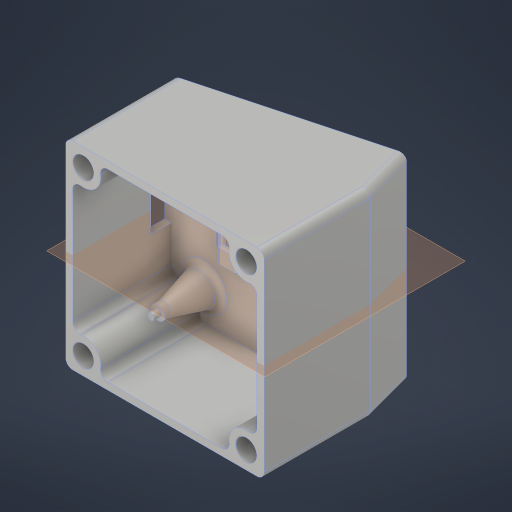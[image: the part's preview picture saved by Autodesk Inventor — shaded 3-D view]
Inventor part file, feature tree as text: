
AUTODESK INVENTOR PART (.ipt)
format: ipt  version: 2023 (Build 270158000, 158)  size: 456,192 bytes
history: native  units: in
note: dims shown in document units (in); Inventor stores cm internally (conversion verified against a paired STEP export)
features: sketch x8, extrude x8, projected_geometry x4, fillet x2, chamfer x2, hole x1, mirror x1, shell x1, plane x1
ambient origin geometry x8: Origin, YZ Plane, XZ Plane, XY Plane, X Axis, Y Axis, Z Axis, Center Point
bodies: Solid1 (feature_tree)
feature tree (28):
  sketch  "Sketch1"  dims[d0=1.4961in d1=1.4961in]
  extrude  "Extrusion1"  Depth=1.4961in
  hole  "Hole1"  [1 undecoded]
  extrude  "Extrusion6"  Depth=0.0787in
  mirror  "Mirror1"
  shell  "Shell1"  Thickness=0.3937in
  extrude  "Extrusion7"  Depth=0.0787in
  fillet  "Fillet1"  Radius=0.1575in
  extrude  "Extrusion2"  Depth=0.1575in
  chamfer  "Chamfer1"  Distance=0.5906in
  extrude  "Extrusion3"  Depth=0.315in
  sketch  "Sketch3"  dims[d5=1.1811in d6=0.0in d7=0.0787in d8=0.3937in]
  extrude  "Extrusion4"  Depth=0.315in
  plane  "Work Plane1"
  extrude  "Extrusion5"  Depth=0.315in
  chamfer  "Chamfer2"  Distance=0.0748in
  fillet  "Fillet3"  Radius=0.0787in
  extrude  "Extrusion8"  Depth=0.315in
  sketch  "Sketch2"  dims[d2=1.3386in d3=1.3386in]
  projected_geometry  "Projected Loop1"
  projected_geometry  "Projected Loop2"
  projected_geometry  "Projected Loop3"
  sketch  "Sketch4"  dims[d9=1.811in]
  sketch  "Sketch5"  dims[d10=0.2283in d11=0.2362in d12=0.385in d13=0.0787in d14=0.5635in d15=0.315in d16=0.8108in d17=0.0787in d18=0.1575in]
  sketch  "Sketch6"  dims[d19=0.1575in d20=0.1575in]
  sketch  "Sketch9"  dims[d21=0.1575in d22=0.5906in d23=0.0in]
  sketch  "Sketch10"  dims[d24=0.1181in d25=0.0787in d26=75.0deg d27=0.0748in d28=0.0748in d29=0.0748in d30=0.0748in d31=0.0787in d32=0.0in d33=0.4724in d34=0.2362in d35=0.0787in d36=1.1811in d37=0.0in d42=0.1969in d43=0.0in d44=0.0197in d45=0.0787in d46=0.481in d47=0.2283in d48=0.2283in d49=0.1969in d50=1.0in d51=0.2756in d52=0.0in d61=0.0787in d62=15.0deg d63=0.3937in d64=0.0in d65=0.0591in d66=0.1969in d67=0.5906in d68=45.0deg d69=45.0deg d70=0.5906in d71=0.1843in d72=0.0591in d73=0.0591in d74=1.5748in d75=1.5748in d76=0.2283in d77=0.2283in d80=0.315in d81=0.0in d82=0.2283in d60=0.0in]
  projected_geometry  "Project Cut Edges1"
note: 1 required parameter value undecoded (feature->parameter linkage not recoverable at this tier; creation-order binding heuristic only, values carry confidence <= 0.55)
